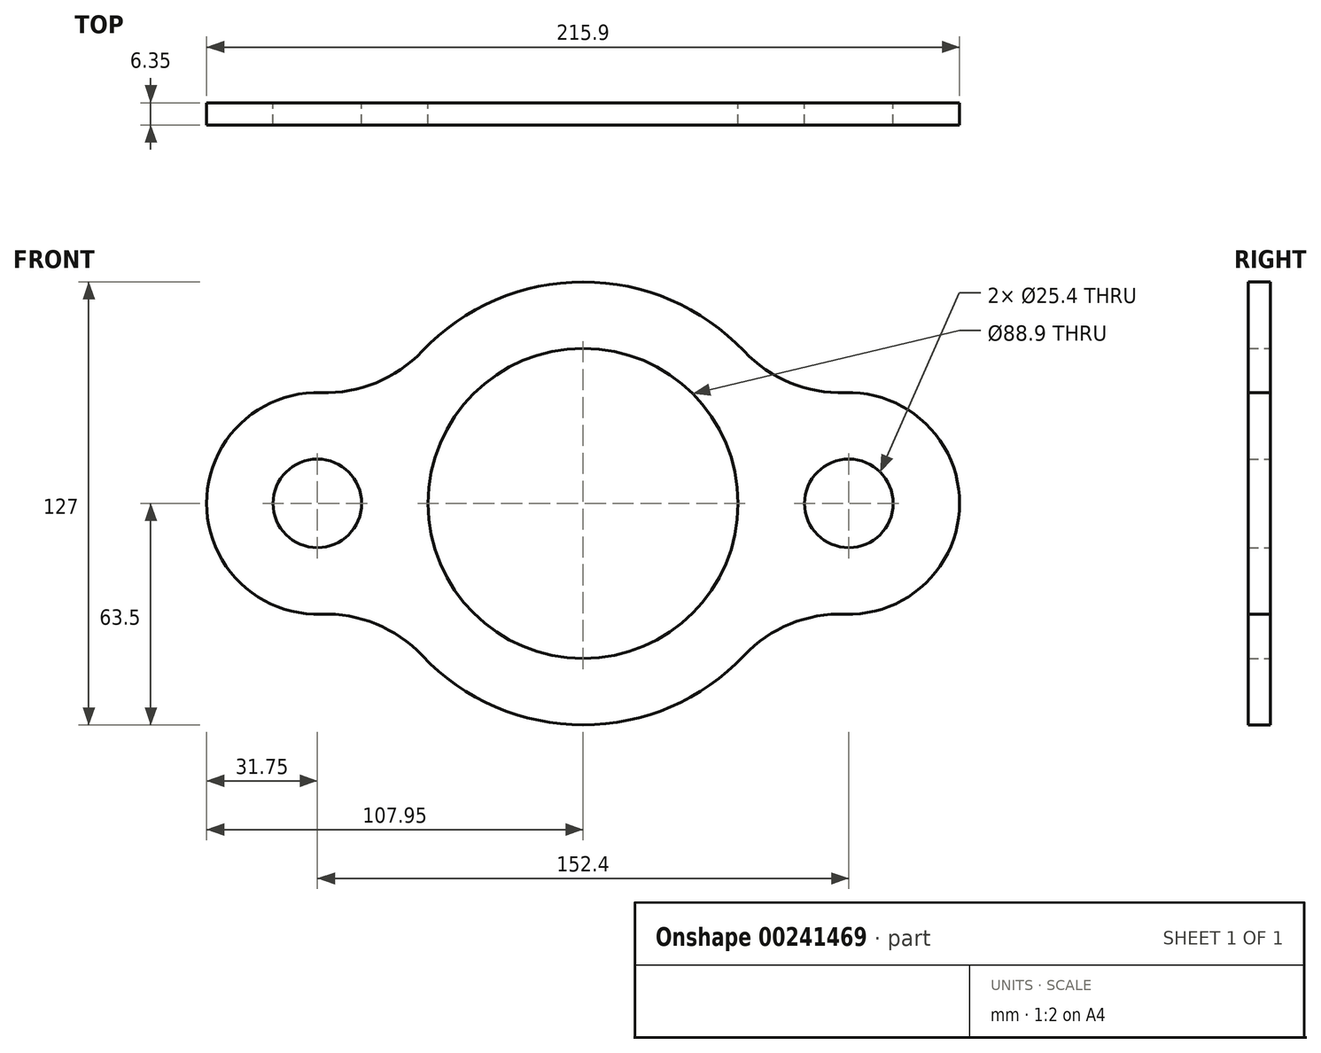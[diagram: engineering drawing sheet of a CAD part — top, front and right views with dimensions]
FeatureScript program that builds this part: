
annotation { "Feature Type Name" : "Feature", "Feature Type Description" : "" }
export const myFeature = defineFeature(function(context is Context, id is Id, definition is map)
    precondition{}
    {
        {
            var Q0;
            Q0=qCreatedBy(makeId("Front.planeOp"),FACE);
            var sketch = newSketch(context, id + "F0", { "sketchPlane" : qUnion([Q0])});
            skCircle(sketch, "E0", {"center": v(0, 0) * mm, "radius": 44.45 * mm});
            skCircle(sketch, "E1", {"center": v(-76.2, 0) * mm, "radius": 12.7 * mm});
            skCircle(sketch, "E2", {"center": v(76.2, 0) * mm, "radius": 12.7 * mm});
            skArc(sketch, "E3", {"start": v(-46.14, -43.63) * mm, "mid": v(0, -63.5) * mm, "end": v(46.14, -43.63) * mm});
            skArc(sketch, "E4", {"start": v(-75.12, 31.73) * mm, "mid": v(-107.95, 0) * mm, "end": v(-75.12, -31.73) * mm});
            skArc(sketch, "E5", {"start": v(75.12, -31.73) * mm, "mid": v(107.95, 0) * mm, "end": v(75.12, 31.73) * mm});
            skArc(sketch, "E6.trimOffspring", {"start": v(46.14, 43.63) * mm, "mid": v(0, 63.5) * mm, "end": v(-46.14, 43.63) * mm});
            skPoint(sketch, "E7.visualSharp", {"position": v(-57.94, 25.98) * mm});
            skArc(sketch, "E7.filletArc", {"start": v(-75.12, 31.73) * mm, "mid": v(-59.35, 34.56) * mm, "end": v(-46.14, 43.63) * mm});
            skPoint(sketch, "E8.visualSharp", {"position": v(57.94, 25.98) * mm});
            skArc(sketch, "E8.filletArc", {"start": v(46.14, 43.63) * mm, "mid": v(59.35, 34.56) * mm, "end": v(75.12, 31.73) * mm});
            skPoint(sketch, "E9.visualSharp", {"position": v(57.94, -25.98) * mm});
            skArc(sketch, "E9.filletArc", {"start": v(75.12, -31.73) * mm, "mid": v(59.35, -34.56) * mm, "end": v(46.14, -43.63) * mm});
            skPoint(sketch, "E10.visualSharp", {"position": v(-57.94, -25.98) * mm});
            skArc(sketch, "E10.filletArc", {"start": v(-46.14, -43.63) * mm, "mid": v(-59.35, -34.56) * mm, "end": v(-75.12, -31.73) * mm});
            skSolve(sketch);
        }
        {
            var Q0;
            Q0=makeQuery(id+"F0.imprint","IMPRINT",FACE,{"disambiguationData":[TD([[makeQuery(id+"F0.imprint","IMPRINT",EDGE,{"derivedFrom":sQuery(id+"F0.wireOp",EDGE,"E0")}),-1.0]])]});
            extrude(context, id + "F1", {"entities" : qUnion([Q0]), "depth" : 6.35 * mm});
        }
    });
